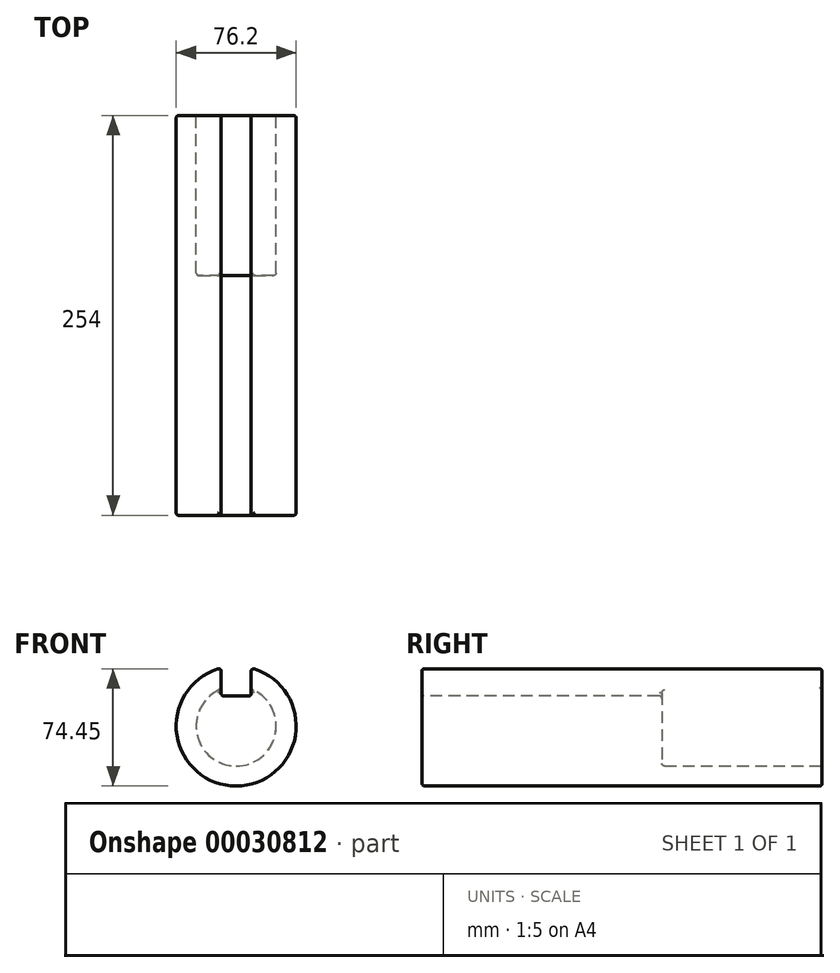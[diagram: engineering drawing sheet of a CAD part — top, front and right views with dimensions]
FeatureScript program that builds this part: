
annotation { "Feature Type Name" : "Feature", "Feature Type Description" : "" }
export const myFeature = defineFeature(function(context is Context, id is Id, definition is map)
    precondition{}
    {
        {
            var Q0;
            Q0=qCreatedBy(makeId("Front.planeOp"),FACE);
            var sketch = newSketch(context, id + "F0", { "sketchPlane" : qUnion([Q0])});
            skCircle(sketch, "E0", {"center": v(0, 0) * mm, "radius": 38.1 * mm});
            skSolve(sketch);
        }
        {
            var Q0;
            Q0 = qSketchRegion(id + "F0", true);
            extrude(context, id + "F1", {"entities" : qUnion([Q0]), "oppositeDirection" : true, "depth" : 254 * mm});
        }
        {
            var Q0;
            Q0=makeQuery(id+"F1.opExtrude","CAP_FACE",FACE,{"disambiguationData":[OSD([sQuery(id+"F0.wireOp",EDGE,"E0")])],"isStart":false});
            var sketch = newSketch(context, id + "F2", { "sketchPlane" : qUnion([Q0])});
            skCircle(sketch, "E1", {"center": v(0, 0) * mm, "radius": 25.4 * mm});
            skSolve(sketch);
        }
        {
            var Q0;
            Q0 = qSketchRegion(id + "F2", true);
            extrude(context, id + "F3", {"entities" : qUnion([Q0]), "operationType" : NewBodyOperationType.REMOVE, "oppositeDirection" : true, "depth" : 101.6 * mm});
        }
        {
            var Q0;
            Q0=qCreatedBy(makeId("Front.planeOp"),FACE);
            var sketch = newSketch(context, id + "F4", { "sketchPlane" : qUnion([Q0])});
            skLineSegment(sketch, "E2.rect.bottom", {"start": v(-9.53, 57.15) * mm, "end": v(9.53, 57.15) * mm});
            skLineSegment(sketch, "E2.rect.top", {"start": v(-9.53, 19.05) * mm, "end": v(9.52, 19.05) * mm});
            skLineSegment(sketch, "E2.rect.left", {"start": v(-9.53, 57.15) * mm, "end": v(-9.53, 19.05) * mm});
            skLineSegment(sketch, "E2.rect.right", {"start": v(9.53, 57.15) * mm, "end": v(9.52, 19.05) * mm});
            skPoint(sketch, "E2.rect.middle", {"position": v(0, 38.1) * mm});
            skSolve(sketch);
        }
        {
            var Q0;
            Q0 = qSketchRegion(id + "F4", true);
            extrude(context, id + "F5", {"entities" : qUnion([Q0]), "operationType" : NewBodyOperationType.REMOVE, "endBound" : BoundingType.THROUGH_ALL, "oppositeDirection" : true, "depth" : 25.4 * mm});
        }
        {
            var Q0;
            Q0=makeQuery(id+"F3.boolean.opBoolean","COPY",EDGE,{"derivedFrom":makeQuery(id+"F3.opExtrude","CAP_EDGE",EDGE,{"disambiguationData":[OSD([sQuery(id+"F2.wireOp",EDGE,"E1")])],"isStart":true})});
            var Q1;
            Q1=makeQuery(id+"F1.opExtrude","CAP_EDGE",EDGE,{"disambiguationData":[OSD([sQuery(id+"F0.wireOp",EDGE,"E0")])],"isStart":false});
            var Q2;
            Q2=makeQuery(id+"F1.opExtrude","CAP_EDGE",EDGE,{"disambiguationData":[OSD([sQuery(id+"F0.wireOp",EDGE,"E0")])],"isStart":true});
            var Q3;
            Q3=makeQuery(id+"F5.boolean.opBoolean","INTERSECT",EDGE,{"derivedFrom":[makeQuery(id+"F3.boolean.opBoolean","COPY",FACE,{"derivedFrom":makeQuery(id+"F3.opExtrude","SWEPT_FACE",FACE,{"disambiguationData":[OSD([sQuery(id+"F2.wireOp",EDGE,"E1")])]})}),makeQuery(id+"F5.opExtrude","SWEPT_FACE",FACE,{"disambiguationData":[OSD([sQuery(id+"F4.wireOp",EDGE,"E2.rect.right")])]})]});
            var Q4;
            Q4=makeQuery(id+"F5.boolean.opBoolean","INTERSECT",EDGE,{"derivedFrom":[makeQuery(id+"F1.opExtrude","SWEPT_FACE",FACE,{"disambiguationData":[OSD([sQuery(id+"F0.wireOp",EDGE,"E0")])]}),makeQuery(id+"F5.opExtrude","SWEPT_FACE",FACE,{"disambiguationData":[OSD([sQuery(id+"F4.wireOp",EDGE,"E2.rect.right")])]})]});
            var Q5;
            Q5=makeQuery(id+"F5.boolean.opBoolean","INTERSECT",EDGE,{"derivedFrom":[makeQuery(id+"F1.opExtrude","CAP_FACE",FACE,{"disambiguationData":[OSD([sQuery(id+"F0.wireOp",EDGE,"E0")])],"isStart":false}),makeQuery(id+"F5.opExtrude","SWEPT_FACE",FACE,{"disambiguationData":[OSD([sQuery(id+"F4.wireOp",EDGE,"E2.rect.right")])]})]});
            var Q6;
            Q6=makeQuery(id+"F5.boolean.opBoolean","INTERSECT",EDGE,{"derivedFrom":[makeQuery(id+"F1.opExtrude","SWEPT_FACE",FACE,{"disambiguationData":[OSD([sQuery(id+"F0.wireOp",EDGE,"E0")])]}),makeQuery(id+"F5.opExtrude","SWEPT_FACE",FACE,{"disambiguationData":[OSD([sQuery(id+"F4.wireOp",EDGE,"E2.rect.left")])]})]});
            var Q7;
            Q7=makeQuery(id+"F5.boolean.opBoolean","INTERSECT",EDGE,{"derivedFrom":[makeQuery(id+"F3.boolean.opBoolean","COPY",FACE,{"derivedFrom":makeQuery(id+"F3.opExtrude","CAP_FACE",FACE,{"disambiguationData":[OSD([sQuery(id+"F2.wireOp",EDGE,"E1")])],"isStart":false})}),makeQuery(id+"F5.opExtrude","SWEPT_FACE",FACE,{"disambiguationData":[OSD([sQuery(id+"F4.wireOp",EDGE,"E2.rect.right")])]})]});
            var Q8;
            Q8=makeQuery(id+"F5.boolean.opBoolean","INTERSECT",EDGE,{"derivedFrom":[makeQuery(id+"F1.opExtrude","CAP_FACE",FACE,{"disambiguationData":[OSD([sQuery(id+"F0.wireOp",EDGE,"E0")])],"isStart":false}),makeQuery(id+"F5.opExtrude","SWEPT_FACE",FACE,{"disambiguationData":[OSD([sQuery(id+"F4.wireOp",EDGE,"E2.rect.left")])]})]});
            var Q9;
            Q9=makeQuery(id+"F5.boolean.opBoolean","COPY",EDGE,{"derivedFrom":makeQuery(id+"F5.opExtrude","CAP_EDGE",EDGE,{"disambiguationData":[OSD([sQuery(id+"F4.wireOp",EDGE,"E2.rect.right")])],"isStart":true})});
            var Q10;
            Q10=makeQuery(id+"F5.boolean.opBoolean","COPY",EDGE,{"derivedFrom":makeQuery(id+"F5.opExtrude","CAP_EDGE",EDGE,{"disambiguationData":[OSD([sQuery(id+"F4.wireOp",EDGE,"E2.rect.left")])],"isStart":true})});
            var Q11;
            Q11=makeQuery(id+"F5.boolean.opBoolean","COPY",EDGE,{"derivedFrom":makeQuery(id+"F5.opExtrude","CAP_EDGE",EDGE,{"disambiguationData":[OSD([sQuery(id+"F4.wireOp",EDGE,"E2.rect.top")])],"isStart":true})});
            var Q12;
            Q12=makeQuery(id+"F5.boolean.opBoolean","COPY",EDGE,{"derivedFrom":makeQuery(id+"F5.opExtrude","SWEPT_EDGE",EDGE,{"disambiguationData":[OSD([sQuery(id+"F4.wireOp",EDGE,"E2.rect.top"),sQuery(id+"F4.wireOp",EDGE,"E2.rect.right")])]})});
            var Q13;
            Q13=makeQuery(id+"F3.boolean.opBoolean","COPY",EDGE,{"derivedFrom":makeQuery(id+"F3.opExtrude","CAP_EDGE",EDGE,{"disambiguationData":[OSD([sQuery(id+"F2.wireOp",EDGE,"E1")])],"isStart":false})});
            var Q14;
            Q14=makeQuery(id+"F5.boolean.opBoolean","INTERSECT",EDGE,{"derivedFrom":[makeQuery(id+"F3.boolean.opBoolean","COPY",FACE,{"derivedFrom":makeQuery(id+"F3.opExtrude","SWEPT_FACE",FACE,{"disambiguationData":[OSD([sQuery(id+"F2.wireOp",EDGE,"E1")])]})}),makeQuery(id+"F5.opExtrude","SWEPT_FACE",FACE,{"disambiguationData":[OSD([sQuery(id+"F4.wireOp",EDGE,"E2.rect.left")])]})]});
            var Q15;
            Q15=makeQuery(id+"F5.boolean.opBoolean","COPY",EDGE,{"derivedFrom":makeQuery(id+"F5.opExtrude","SWEPT_EDGE",EDGE,{"disambiguationData":[OSD([sQuery(id+"F4.wireOp",EDGE,"E2.rect.top"),sQuery(id+"F4.wireOp",EDGE,"E2.rect.left")])]})});
            var Q16;
            Q16=makeQuery(id+"F5.boolean.opBoolean","INTERSECT",EDGE,{"derivedFrom":[makeQuery(id+"F3.boolean.opBoolean","COPY",FACE,{"derivedFrom":makeQuery(id+"F3.opExtrude","CAP_FACE",FACE,{"disambiguationData":[OSD([sQuery(id+"F2.wireOp",EDGE,"E1")])],"isStart":false})}),makeQuery(id+"F5.opExtrude","SWEPT_FACE",FACE,{"disambiguationData":[OSD([sQuery(id+"F4.wireOp",EDGE,"E2.rect.left")])]})]});
            var Q17;
            Q17=makeQuery(id+"F5.boolean.opBoolean","INTERSECT",EDGE,{"derivedFrom":[makeQuery(id+"F3.boolean.opBoolean","COPY",FACE,{"derivedFrom":makeQuery(id+"F3.opExtrude","CAP_FACE",FACE,{"disambiguationData":[OSD([sQuery(id+"F2.wireOp",EDGE,"E1")])],"isStart":false})}),makeQuery(id+"F5.opExtrude","SWEPT_FACE",FACE,{"disambiguationData":[OSD([sQuery(id+"F4.wireOp",EDGE,"E2.rect.top")])]})]});
            fillet(context, id + "F6", {"entities" : qUnion([Q0, Q1, Q2, Q3, Q4, Q5, Q6, Q7, Q8, Q9, Q10, Q11, Q12, Q13, Q14, Q15, Q16, Q17]), "radius" : 1.65 * mm, "tangentPropagation" : true, "allowEdgeOverflow" : false});
        }
    });
